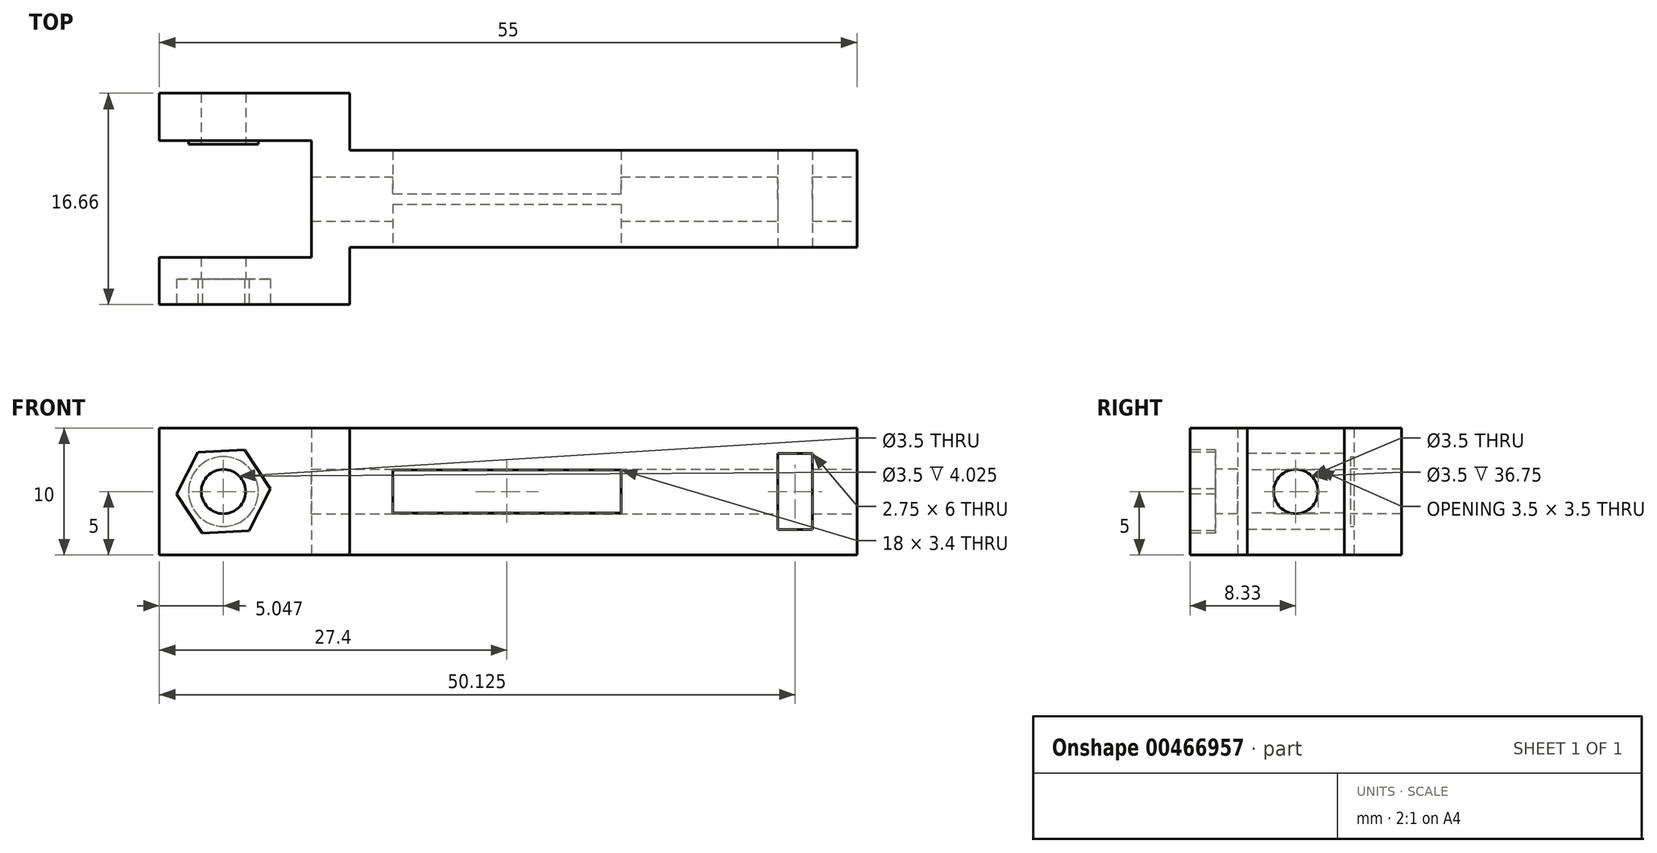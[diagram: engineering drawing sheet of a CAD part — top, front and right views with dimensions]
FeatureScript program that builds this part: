
annotation { "Feature Type Name" : "Feature", "Feature Type Description" : "" }
export const myFeature = defineFeature(function(context is Context, id is Id, definition is map)
    precondition{}
    {
        {
            var Q0;
            Q0=qCreatedBy(makeId("Top.planeOp"),FACE);
            var sketch = newSketch(context, id + "F0", { "sketchPlane" : qUnion([Q0])});
            skLineSegment(sketch, "E0.bottom", {"start": v(0, 0) * mm, "end": v(40, 0) * mm});
            skLineSegment(sketch, "E0.top", {"start": v(0, -3.83) * mm, "end": v(40, -3.83) * mm});
            skLineSegment(sketch, "E0.left", {"start": v(0, 0) * mm, "end": v(0, -3.83) * mm});
            skLineSegment(sketch, "E0.right", {"start": v(40, 0) * mm, "end": v(40, -3.83) * mm});
            skLineSegment(sketch, "E1.bottom", {"start": v(-3, 0) * mm, "end": v(0, 0) * mm});
            skLineSegment(sketch, "E1.top", {"start": v(-15, -8.32) * mm, "end": v(0, -8.32) * mm});
            skLineSegment(sketch, "E1.left", {"start": v(-15, -4.6) * mm, "end": v(-15, -8.32) * mm});
            skLineSegment(sketch, "E1.right", {"start": v(0, 0) * mm, "end": v(0, -8.32) * mm});
            skLineSegment(sketch, "E2.top", {"start": v(-15, -4.6) * mm, "end": v(-3, -4.6) * mm});
            skLineSegment(sketch, "E2.right", {"start": v(-3, 0) * mm, "end": v(-3, -4.6) * mm});
            skLineSegment(sketch, "E3.MirrorCS", {"start": v(0, 0) * mm, "end": v(0, 3.83) * mm});
            skLineSegment(sketch, "E4.MirrorCS", {"start": v(0, 0) * mm, "end": v(0, 8.32) * mm});
            skLineSegment(sketch, "E5.MirrorCS", {"start": v(-15, 4.6) * mm, "end": v(-15, 8.32) * mm});
            skLineSegment(sketch, "E6.MirrorCS", {"start": v(-3, 0) * mm, "end": v(-3, 4.6) * mm});
            skLineSegment(sketch, "E7.MirrorCS", {"start": v(-15, 8.32) * mm, "end": v(0, 8.32) * mm});
            skLineSegment(sketch, "E8.MirrorCS", {"start": v(-15, 4.6) * mm, "end": v(-3, 4.6) * mm});
            skLineSegment(sketch, "E9.MirrorCS", {"start": v(40, 0) * mm, "end": v(40, 3.83) * mm});
            skLineSegment(sketch, "E10.MirrorCS", {"start": v(0, 3.83) * mm, "end": v(40, 3.83) * mm});
            skSolve(sketch);
        }
        {
            var Q0;
            {var subQ2=sQuery(id+"F0.wireOp",EDGE,"E1.top");Q0=makeQuery(id+"F0.imprint","IMPRINT",FACE,{"disambiguationData":[TD([[makeQuery(id+"F0.imprint","IMPRINT",EDGE,{"derivedFrom":subQ2}),1.0]])]});}
            var Q1;
            Q1=makeQuery(id+"F0.imprint","IMPRINT",FACE,{"disambiguationData":[TD([[makeQuery(id+"F0.imprint","IMPRINT",EDGE,{"derivedFrom":sQuery(id+"F0.wireOp",EDGE,"E5.MirrorCS")}),-1.0]])]});
            var Q2;
            {var subQ0=sQuery(id+"F0.wireOp",EDGE,"E0.bottom");Q2=makeQuery(id+"F0.imprint","IMPRINT",FACE,{"disambiguationData":[TD([[makeQuery(id+"F0.imprint","IMPRINT",EDGE,{"derivedFrom":subQ0}),1.0]])]});}
            var Q3;
            {var subQ0=sQuery(id+"F0.wireOp",EDGE,"E0.bottom");Q3=makeQuery(id+"F0.imprint","IMPRINT",FACE,{"disambiguationData":[TD([[makeQuery(id+"F0.imprint","IMPRINT",EDGE,{"derivedFrom":subQ0}),-1.0]])]});}
            extrude(context, id + "F1", {"entities" : qUnion([Q0, Q1, Q2, Q3]), "depth" : 10 * mm});
        }
        {
            var Q0;
            Q0=makeQuery(id+"F1.opExtrude","SWEPT_FACE",FACE,{"disambiguationData":[OSD([sQuery(id+"F0.wireOp",EDGE,"E1.top")])]});
            var sketch = newSketch(context, id + "F2", { "sketchPlane" : qUnion([Q0])});
            skCircle(sketch, "E11", {"center": v(-9.95, 5) * mm, "radius": 1.75 * mm});
            skSolve(sketch);
        }
        {
            var Q0;
            Q0=makeQuery(id+"F2.imprint","IMPRINT",FACE,{"disambiguationData":[TD([[makeQuery(id+"F2.imprint","IMPRINT",EDGE,{"derivedFrom":sQuery(id+"F2.wireOp",EDGE,"E11")}),1.0]])]});
            extrude(context, id + "F3", {"entities" : qUnion([Q0]), "operationType" : NewBodyOperationType.REMOVE, "endBound" : BoundingType.THROUGH_ALL, "oppositeDirection" : true, "depth" : 25 * mm});
        }
        {
            var Q0;
            Q0=makeQuery(id+"F1.opExtrude","SWEPT_FACE",FACE,{"disambiguationData":[OSD([sQuery(id+"F0.wireOp",EDGE,"E0.top")])]});
            var sketch = newSketch(context, id + "F4", { "sketchPlane" : qUnion([Q0])});
            skLineSegment(sketch, "E12.bottom", {"start": v(3.4, 3.3) * mm, "end": v(21.4, 3.3) * mm});
            skLineSegment(sketch, "E12.top", {"start": v(3.4, 6.7) * mm, "end": v(21.4, 6.7) * mm});
            skLineSegment(sketch, "E12.left", {"start": v(3.4, 3.3) * mm, "end": v(3.4, 6.7) * mm});
            skLineSegment(sketch, "E12.right", {"start": v(21.4, 3.3) * mm, "end": v(21.4, 6.7) * mm});
            skLineSegment(sketch, "E13.bottom", {"start": v(33.75, 8) * mm, "end": v(36.5, 8) * mm});
            skLineSegment(sketch, "E13.top", {"start": v(33.75, 2) * mm, "end": v(36.5, 2) * mm});
            skLineSegment(sketch, "E13.left", {"start": v(33.75, 8) * mm, "end": v(33.75, 2) * mm});
            skLineSegment(sketch, "E13.right", {"start": v(36.5, 8) * mm, "end": v(36.5, 2) * mm});
            skSolve(sketch);
        }
        {
            var Q0;
            Q0=makeQuery(id+"F4.imprint","IMPRINT",FACE,{"disambiguationData":[TD([[makeQuery(id+"F4.imprint","IMPRINT",EDGE,{"derivedFrom":sQuery(id+"F4.wireOp",EDGE,"E12.bottom")}),1.0]])]});
            var Q1;
            Q1=makeQuery(id+"F4.imprint","IMPRINT",FACE,{"disambiguationData":[TD([[makeQuery(id+"F4.imprint","IMPRINT",EDGE,{"derivedFrom":sQuery(id+"F4.wireOp",EDGE,"E13.bottom")}),-1.0]])]});
            extrude(context, id + "F5", {"entities" : qUnion([Q0, Q1]), "operationType" : NewBodyOperationType.REMOVE, "endBound" : BoundingType.THROUGH_ALL, "oppositeDirection" : true, "depth" : 25 * mm});
        }
        {
            var Q0;
            Q0=makeQuery(id+"F1.opExtrude","SWEPT_FACE",FACE,{"disambiguationData":[OSD([sQuery(id+"F0.wireOp",EDGE,"E0.right"),sQuery(id+"F0.wireOp",EDGE,"E9.MirrorCS")])]});
            var sketch = newSketch(context, id + "F6", { "sketchPlane" : qUnion([Q0])});
            skCircle(sketch, "E14", {"center": v(0, 5) * mm, "radius": 1.75 * mm});
            skSolve(sketch);
        }
        {
            var Q0;
            Q0=makeQuery(id+"F6.imprint","IMPRINT",FACE,{"disambiguationData":[TD([[makeQuery(id+"F6.imprint","IMPRINT",EDGE,{"derivedFrom":sQuery(id+"F6.wireOp",EDGE,"E14")}),1.0]])]});
            extrude(context, id + "F7", {"entities" : qUnion([Q0]), "operationType" : NewBodyOperationType.REMOVE, "oppositeDirection" : true, "depth" : 15 * mm});
        }
        {
            var Q0;
            Q0=makeQuery(id+"F1.opExtrude","SWEPT_FACE",FACE,{"disambiguationData":[OSD([sQuery(id+"F0.wireOp",EDGE,"E0.right"),sQuery(id+"F0.wireOp",EDGE,"E9.MirrorCS")])]});
            cPlane(context, id + "F8", {"entities" : qUnion([Q0]), "cplaneType" : CPlaneType.OFFSET, "offset" : 5 * mm, "width" : 150 * mm, "height" : 150 * mm});
        }
        {
            var Q0;
            Q0=qCreatedBy(id+"F8.planeOp",FACE);
            var sketch = newSketch(context, id + "F9", { "sketchPlane" : qUnion([Q0])});
            skLineSegment(sketch, "E15.0", {"start": v(3.83, 10) * mm, "end": v(3.83, 0) * mm});
            skLineSegment(sketch, "E16.0", {"start": v(-3.82, 10) * mm, "end": v(-3.82, 0) * mm});
            skLineSegment(sketch, "E17.bottom", {"start": v(-3.82, 19.85) * mm, "end": v(3.83, 19.85) * mm});
            skLineSegment(sketch, "E17.top", {"start": v(-3.82, -10.15) * mm, "end": v(3.83, -10.15) * mm});
            skLineSegment(sketch, "E17.left", {"start": v(-3.82, 19.85) * mm, "end": v(-3.82, -10.15) * mm});
            skLineSegment(sketch, "E17.right", {"start": v(3.83, 19.85) * mm, "end": v(3.83, -10.15) * mm});
            skPoint(sketch, "E18.oppositeSnap0", {"position": v(3.83, 4.85) * mm});
            skLineSegment(sketch, "E18.bottom", {"start": v(3.83, 4.85) * mm, "end": v(3.83, 4.85) * mm});
            skLineSegment(sketch, "E18.top", {"start": v(3.83, 4.85) * mm, "end": v(3.83, 4.85) * mm});
            skLineSegment(sketch, "E18.left", {"start": v(3.83, 4.85) * mm, "end": v(3.83, 4.85) * mm});
            skLineSegment(sketch, "E18.right", {"start": v(3.83, 4.85) * mm, "end": v(3.83, 4.85) * mm});
            skSolve(sketch);
        }
        {
            var Q0;
            {var subQ0=sQuery(id+"F9.wireOp",EDGE,"E17.bottom");Q0=makeQuery(id+"F9.imprint","IMPRINT",FACE,{"disambiguationData":[TD([[makeQuery(id+"F9.imprint","IMPRINT",EDGE,{"derivedFrom":subQ0}),-1.0]])]});}
            extrude(context, id + "F10", {"entities" : qUnion([Q0]), "depth" : 2 * mm});
        }
        {
            var Q0;
            Q0=makeQuery(id+"F10.opExtrude","CAP_FACE",FACE,{"disambiguationData":[OSD([sQuery(id+"F9.wireOp",EDGE,"E17.bottom"),sQuery(id+"F9.wireOp",EDGE,"E17.top"),sQuery(id+"F9.wireOp",EDGE,"E17.left"),sQuery(id+"F9.wireOp",EDGE,"E17.right")])],"isStart":false});
            var sketch = newSketch(context, id + "F11", { "sketchPlane" : qUnion([Q0])});
            skLineSegment(sketch, "E19.bottom", {"start": v(8.82, 34.85) * mm, "end": v(-8.83, 34.85) * mm});
            skLineSegment(sketch, "E19.top", {"start": v(8.83, -25.15) * mm, "end": v(-8.82, -25.15) * mm});
            skLineSegment(sketch, "E19.left", {"start": v(8.82, 34.85) * mm, "end": v(8.83, -25.15) * mm});
            skLineSegment(sketch, "E19.right", {"start": v(-8.83, 34.85) * mm, "end": v(-8.82, -25.15) * mm});
            skSolve(sketch);
        }
        {
            var Q0;
            Q0=qSketchRegion(id+"F11",true);
            extrude(context, id + "F12", {"entities" : qUnion([Q0]), "operationType" : NewBodyOperationType.ADD, "depth" : 8 * mm});
        }
        {
            var Q0;
            Q0=makeQuery(id+"F12.opExtrude","CAP_FACE",FACE,{"disambiguationData":[OSD([sQuery(id+"F11.wireOp",EDGE,"E19.bottom"),sQuery(id+"F11.wireOp",EDGE,"E19.top"),sQuery(id+"F11.wireOp",EDGE,"E19.left"),sQuery(id+"F11.wireOp",EDGE,"E19.right")])],"isStart":false});
            var sketch = newSketch(context, id + "F13", { "sketchPlane" : qUnion([Q0])});
            skCircle(sketch, "E20.0", {"center": v(0, 5) * mm, "radius": 1.75 * mm});
            skSolve(sketch);
        }
        {
            var Q0;
            Q0=makeQuery(id+"F13.imprint","IMPRINT",FACE,{"disambiguationData":[TD([[makeQuery(id+"F13.imprint","IMPRINT",EDGE,{"derivedFrom":sQuery(id+"F13.wireOp",EDGE,"E20.0")}),1.0]])]});
            extrude(context, id + "F14", {"entities" : qUnion([Q0]), "operationType" : NewBodyOperationType.REMOVE, "endBound" : BoundingType.THROUGH_ALL, "oppositeDirection" : true, "depth" : 25 * mm});
        }
        {
            var Q0;
            Q0=makeQuery(id+"F1.opExtrude","SWEPT_FACE",FACE,{"disambiguationData":[OSD([sQuery(id+"F0.wireOp",EDGE,"E8.MirrorCS")])]});
            var sketch = newSketch(context, id + "F15", { "sketchPlane" : qUnion([Q0])});
            skCircle(sketch, "E21", {"center": v(-9.95, 5) * mm, "radius": 1.75 * mm});
            skCircle(sketch, "E22", {"center": v(-9.95, 5) * mm, "radius": 2.75 * mm});
            skSolve(sketch);
        }
        {
            var Q0;
            Q0=makeQuery(id+"F15.imprint","IMPRINT",FACE,{"disambiguationData":[TD([[makeQuery(id+"F15.imprint","IMPRINT",EDGE,{"derivedFrom":sQuery(id+"F15.wireOp",EDGE,"E21")}),1.0]])]});
            extrude(context, id + "F16", {"entities" : qUnion([Q0]), "operationType" : NewBodyOperationType.ADD, "depth" : 0.3 * mm});
        }
        {
            var Q0;
            Q0=makeQuery(id+"F1.opExtrude","SWEPT_FACE",FACE,{"disambiguationData":[OSD([sQuery(id+"F0.wireOp",EDGE,"E1.top")])]});
            var sketch = newSketch(context, id + "F17", { "sketchPlane" : qUnion([Q0])});
            skCircle(sketch, "E23.cCircle", {"center": v(-9.95, 5) * mm, "radius": 3.2 * mm, "construction": true});
            skLineSegment(sketch, "E23.0", {"start": v(-6.26, 5.2) * mm, "end": v(-7.93, 1.9) * mm});
            skLineSegment(sketch, "E23.1", {"start": v(-7.93, 1.9) * mm, "end": v(-11.62, 1.7) * mm});
            skLineSegment(sketch, "E23.2", {"start": v(-11.62, 1.7) * mm, "end": v(-13.64, 4.8) * mm});
            skLineSegment(sketch, "E23.3", {"start": v(-13.64, 4.8) * mm, "end": v(-11.98, 8.1) * mm});
            skLineSegment(sketch, "E23.4", {"start": v(-11.98, 8.1) * mm, "end": v(-8.29, 8.3) * mm});
            skLineSegment(sketch, "E23.5", {"start": v(-8.29, 8.3) * mm, "end": v(-6.26, 5.2) * mm});
            skPoint(sketch, "E23.0.midPoint", {"position": v(-7.1, 3.56) * mm});
            skSolve(sketch);
        }
        {
            var Q0;
            Q0=makeQuery(id+"F17.imprint","IMPRINT",FACE,{"disambiguationData":[TD([[makeQuery(id+"F17.imprint","IMPRINT",EDGE,{"derivedFrom":sQuery(id+"F17.wireOp",EDGE,"E23.0")}),-1.0]])]});
            extrude(context, id + "F18", {"entities" : qUnion([Q0]), "operationType" : NewBodyOperationType.REMOVE, "oppositeDirection" : true, "depth" : 2 * mm});
        }
        {
            var Q0;
            Q0=makeQuery(id+"F12.opExtrude","CAP_FACE",FACE,{"disambiguationData":[OSD([sQuery(id+"F11.wireOp",EDGE,"E19.bottom"),sQuery(id+"F11.wireOp",EDGE,"E19.top"),sQuery(id+"F11.wireOp",EDGE,"E19.left"),sQuery(id+"F11.wireOp",EDGE,"E19.right")])],"isStart":true});
            var sketch = newSketch(context, id + "F19", { "sketchPlane" : qUnion([Q0])});
            skCircle(sketch, "E24.0", {"center": v(0, 5) * mm, "radius": 1.75 * mm});
            skCircle(sketch, "E25", {"center": v(0, -18) * mm, "radius": 3.75 * mm});
            skCircle(sketch, "E26", {"center": v(0, 28) * mm, "radius": 3.75 * mm});
            skSolve(sketch);
        }
        {
            var Q0;
            Q0=makeQuery(id+"F19.imprint","IMPRINT",FACE,{"disambiguationData":[TD([[makeQuery(id+"F19.imprint","IMPRINT",EDGE,{"derivedFrom":sQuery(id+"F19.wireOp",EDGE,"E25")}),1.0]])]});
            var Q1;
            Q1=makeQuery(id+"F19.imprint","IMPRINT",FACE,{"disambiguationData":[TD([[makeQuery(id+"F19.imprint","IMPRINT",EDGE,{"derivedFrom":sQuery(id+"F19.wireOp",EDGE,"E26")}),1.0]])]});
            extrude(context, id + "F20", {"entities" : qUnion([Q0, Q1]), "operationType" : NewBodyOperationType.ADD, "depth" : 1 * mm});
        }
        {
            var Q0;
            Q0=makeQuery(id+"F10.opExtrude","SWEPT_BODY",BODY,{"disambiguationData":[OSD([sQuery(id+"F9.wireOp",EDGE,"E17.bottom"),sQuery(id+"F9.wireOp",EDGE,"E17.top"),sQuery(id+"F9.wireOp",EDGE,"E17.left"),sQuery(id+"F9.wireOp",EDGE,"E17.right")])]});
            deleteBodies(context, id + "F21", {"entities" : qUnion([Q0])});
        }
    });
